# Revit family: Domotics-DomesticRanges-GEWISS-CHORUS_POWER-SOCKET-OUTLET_AUS
name_source: partatom
category: Apparecchi elettrici
revit_build: Autodesk Revit 2016 (Build: 20161004_0715(x64)
units: mm (PartAtom-declared; Revit-internal decimal feet)

## family parameters
Condiviso = Sì
Host = Superficie
Mantenere orientamento annotazione = Sì
Punto di calcolo locali = Sì
Quota connettore circolare = Usa diametro
Taglio con vuoti quando caricato = Sì
Tipo di parte = Normale

## types (6) — shared parameters
Breaking capacity: = 1.25 In (100 position changes)
Carico apparente = 0 VA
Catalogue = DOMOTICS
Catalogue Range = CHORUS - DOMESTIC RANGE
Category = Socket-outlet
Description. = Socket-outlet
Electrocod = 0131
Finitura = GEWISS TITANIO
For plug pins = Flat
Glow Wire Test = 850°C
IDF = 73681ca5-b756-4457-b06b-a96d388490b1
IDT = 50b4fa2c-1c23-451b-8599-15baeb98b52f
Immagine tipo = GW14307.jpg
Insulation resistance = > 5 MOhm
N. poli = 1
No. Chorus modules = 2
No. Chorus modules: = 2
Produttore = GEWISS S.p.A.
Prolonged operation (no.of position changes) = 10.000 at In 250 V ac cosÃ˜=0,8
Prospetto di default = 1219 mm
Resistance at test voltage = 2000 V at 50 Hz for 1 minute
SEO = Socket outlet
Standard = Australian
Standard: = Australian
Standard; = IEC 60884-1; AS/NZS 3112
TIPO_ = Chorus Prese Australia_GENERICO : GW14307 Presa 2M 2P+T 15A standard Australiano titanio
TXT ELETTRICO = 15
Technical sheet = https://www.gewiss.com
Terminal grip on cable traction = > 50 N
Terminal tightening capacity flexible cables (mm2) = min. 0,75 - max. 2x4
Terminal tightening capacity rigid cables (mm2) = min. 0,5 - max. 2x2,5
Thermo-pressure with ball = 125
URL = https://www.gewiss.com
Version file RFA = 19.0
Volt = 230 V
Voltage = 250 V ac
Voltage: = 250 V ac
Wiring terminals = With screw

## per-type parameters (varying)
| type | Colour | Description: | Descrizione | EAN code | Modello |
| GW12307 - Socket outlet 2M 2P+E 15A australian standard black | Black | 2P+E - 15A | SOCKET 2M 2P+E 15A AUS STANDARD BLACK | 8011564267008 | GW12307 |
| GW10306 - Socket outlet 2M 2P+E 10A australian standard white | White | 2P+E - 10A | S. OUTLET 2M 2P+E 10A AUS ST WHITE | 8011564258020 | GW10306 |
| GW10307 - Socket outlet 2M 2P+E 10A australian standard white | White | 2P+E - 15A | S. OUTLET 2M 2P+E 15A AUS ST WHITE | 8011564258037 | GW10307 |
| GW14306 - Socket outlet 2M 2P+E 10A australian standard titanium | Titanium | 2P+E - 10A | SOCKET 2M 2P+E 10A AUS STANDARD TITANIUM | 8011564266476 | GW14306 |
| GW14307 - Socket outlet 2M 2P+E 15A australian standard titanium | Titanium | 2P+E - 15A | SOCKET 2M 2P+E 15A AUS STANDARD TITANIUM | 8011564266483 | GW14307 |
| GW12306 - Socket outlet 2M 2P+E 15A australian standard black | Black | 2P+E - 10A | SOCKET 2M 2P+E 10A AUS STANDARD BLACK | 8011564266995 | GW12306 |

note: source unit labels omitted for Thermo-pressure with ball — the stored unit's dimension contradicts the parameter name (converter mislabeling)

## geometry (parser evidence)
native form markers: Sweep x2
no freeform markers — native parametric forms only
